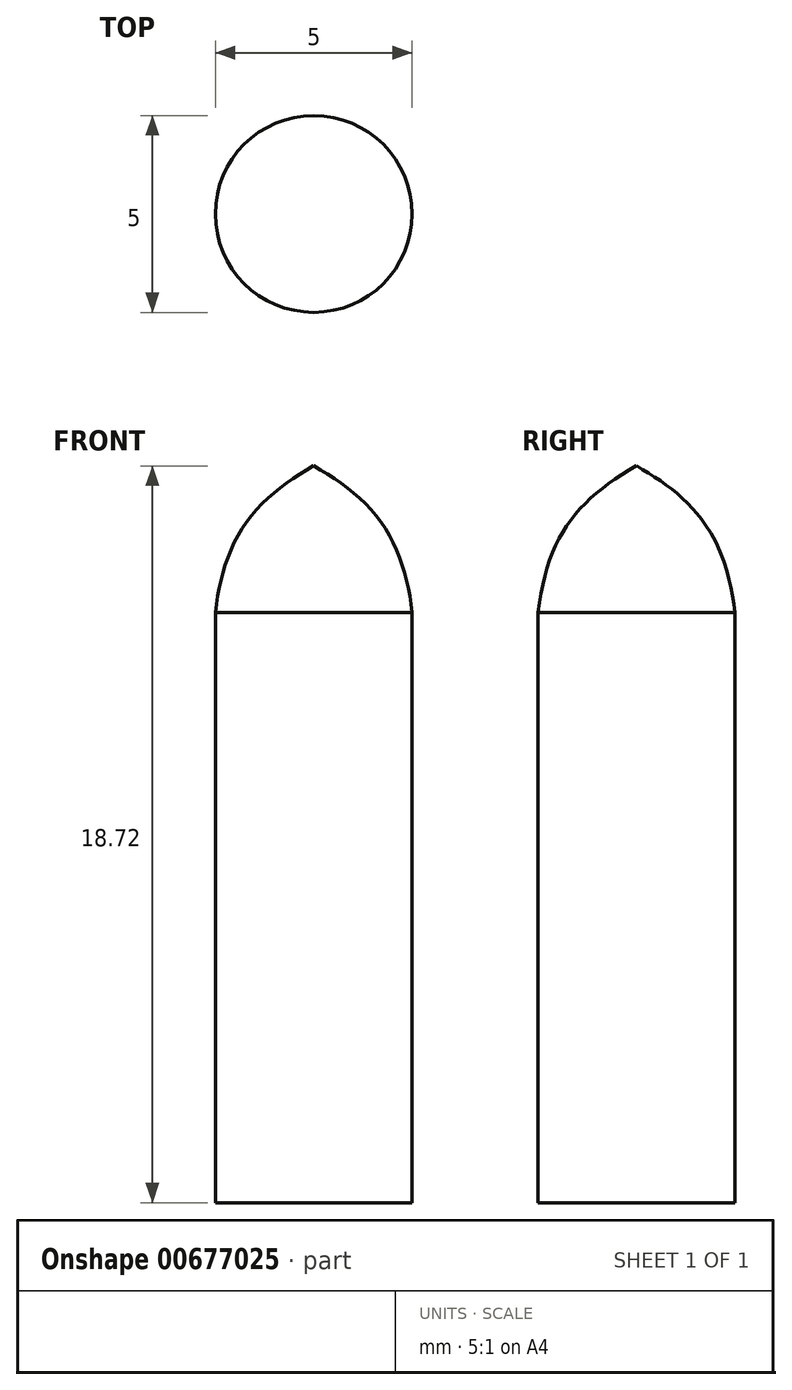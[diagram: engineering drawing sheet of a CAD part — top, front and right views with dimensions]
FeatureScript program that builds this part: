
annotation { "Feature Type Name" : "Feature", "Feature Type Description" : "" }
export const myFeature = defineFeature(function(context is Context, id is Id, definition is map)
    precondition{}
    {
        {
            var Q0;
            Q0=qCreatedBy(makeId("Top.planeOp"),FACE);
            var sketch = newSketch(context, id + "F0", { "sketchPlane" : qUnion([Q0])});
            skCircle(sketch, "E0", {"center": v(0, 0) * mm, "radius": 2.5 * mm});
            skSolve(sketch);
        }
        {
            var Q0;
            Q0=makeQuery(id+"F0.imprint","IMPRINT",FACE,{"disambiguationData":[TD([[makeQuery(id+"F0.imprint","IMPRINT",EDGE,{"derivedFrom":sQuery(id+"F0.wireOp",EDGE,"E0")}),1.0]])]});
            var Q1;
            Q1=sQuery(id+"F0.wireOp",EDGE,"E0");
            extrude(context, id + "F1", {"entities" : qUnion([Q0]), "surfaceEntities" : qUnion([Q1]), "depth" : 15 * mm, "offsetDistance" : 25.4 * mm});
        }
        {
            var Q0;
            Q0=makeQuery(id+"F1.opExtrude","CAP_FACE",FACE,{"disambiguationData":[OSD([sQuery(id+"F0.wireOp",EDGE,"E0")])],"isStart":false});
            var sketch = newSketch(context, id + "F2", { "sketchPlane" : qUnion([Q0])});
            skPoint(sketch, "E1", {"position": v(0, -2.5) * mm});
            skPoint(sketch, "E2", {"position": v(0, 2.5) * mm});
            skSolve(sketch);
        }
        {
            var Q0;
            Q0=qCreatedBy(makeId("Right.planeOp"),FACE);
            var sketch = newSketch(context, id + "F3", { "sketchPlane" : qUnion([Q0])});
            skFitSpline(sketch, "E3", {"points": [v(-2.5, 15) * mm, v(0, 18.72) * mm], "startDerivative": vector(0.68, 5.8) * mm, "endDerivative": vector(4.45, 2.53) * mm});
            skLineSegment(sketch, "E4", {"start": v(0, 18.72) * mm, "end": v(0, 15) * mm});
            skLineSegment(sketch, "E5", {"start": v(0, 15) * mm, "end": v(-2.5, 15) * mm});
            skSolve(sketch);
        }
        {
            var Q0;
            Q0=makeQuery(id+"F3.imprint","IMPRINT",FACE,{"disambiguationData":[TD([[makeQuery(id+"F3.imprint","IMPRINT",EDGE,{"derivedFrom":sQuery(id+"F3.wireOp",EDGE,"E3")}),-1.0]])]});
            var Q1;
            Q1=sQuery(id+"F3.wireOp",EDGE,"E4");
            revolve(context, id + "F4", {"operationType" : NewBodyOperationType.ADD, "entities" : qUnion([Q0]), "axis" : qUnion([Q1]), "revolveType" : RevolveType.FULL});
        }
    });
